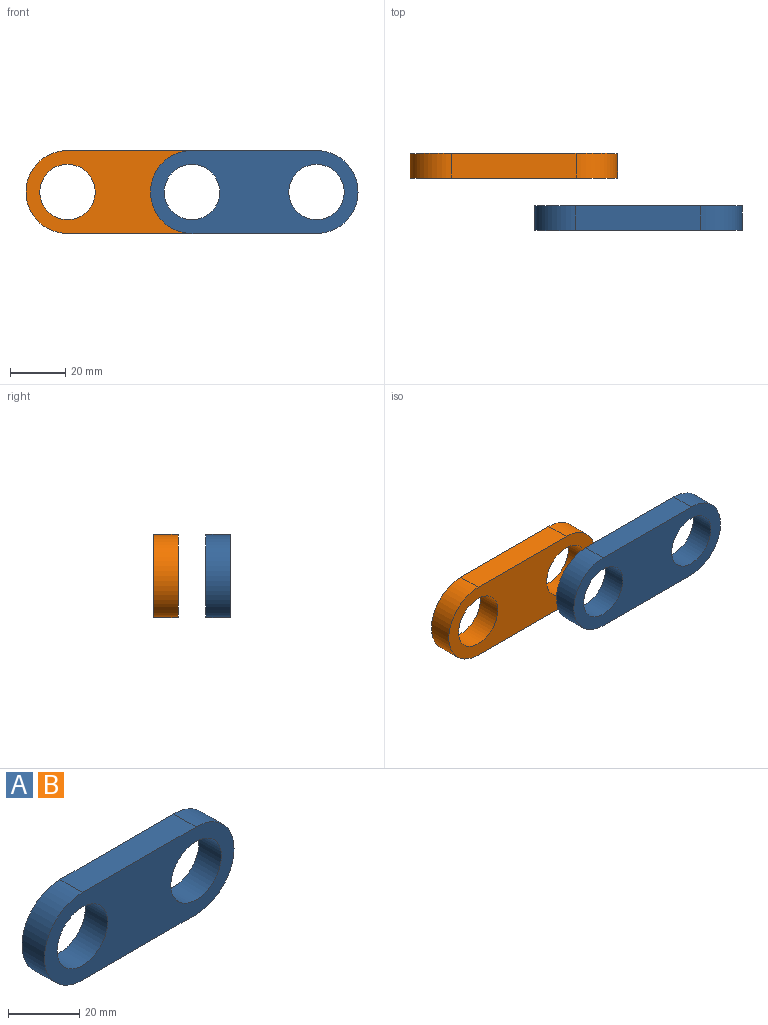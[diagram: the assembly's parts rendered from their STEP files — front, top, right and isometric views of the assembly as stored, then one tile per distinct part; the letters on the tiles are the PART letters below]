
ASSEMBLY  parts=2 mates=1
PART A: 8 faces, bbox 75x8.9x30 mm
  f0: plane 45x8.9mm, normal (0,0,-1), area 400.5mm2, adj f1,f5,f6,f7
  f1: cylinder r=15mm len=30mm, axis (0,1,0), area 419.4mm2, adj f0,f2,f6,f7
  f2: plane 45x8.9mm, normal (0,0,1), area 400.5mm2, adj f1,f5,f6,f7
  f3: cylinder r=10mm len=20mm, axis (0,1,0), area 559.2mm2, adj f6,f7
  f4: cylinder r=10mm len=20mm, axis (0,1,0), area 559.2mm2, adj f6,f7
  f5: cylinder r=15mm len=30mm, axis (0,1,0), area 419.4mm2, adj f0,f2,f6,f7
  f6: plane 75x30mm, normal (0,-1,0), area 1428.5mm2, adj f0,f1,f2,f3,f4,f5
  f7: plane 75x30mm, normal (0,1,0), area 1428.5mm2, adj f0,f1,f2,f3,f4,f5
PART B: same geometry as A
PLACE A t=(61.28,-16.75,-22.99)mm
PLACE B t=(16.28,2.15,-22.99)mm
MATE revolute B.f1 <-> A.f3  axis (0,-1,0) through (17.58,-16.75,-28.85)mm
